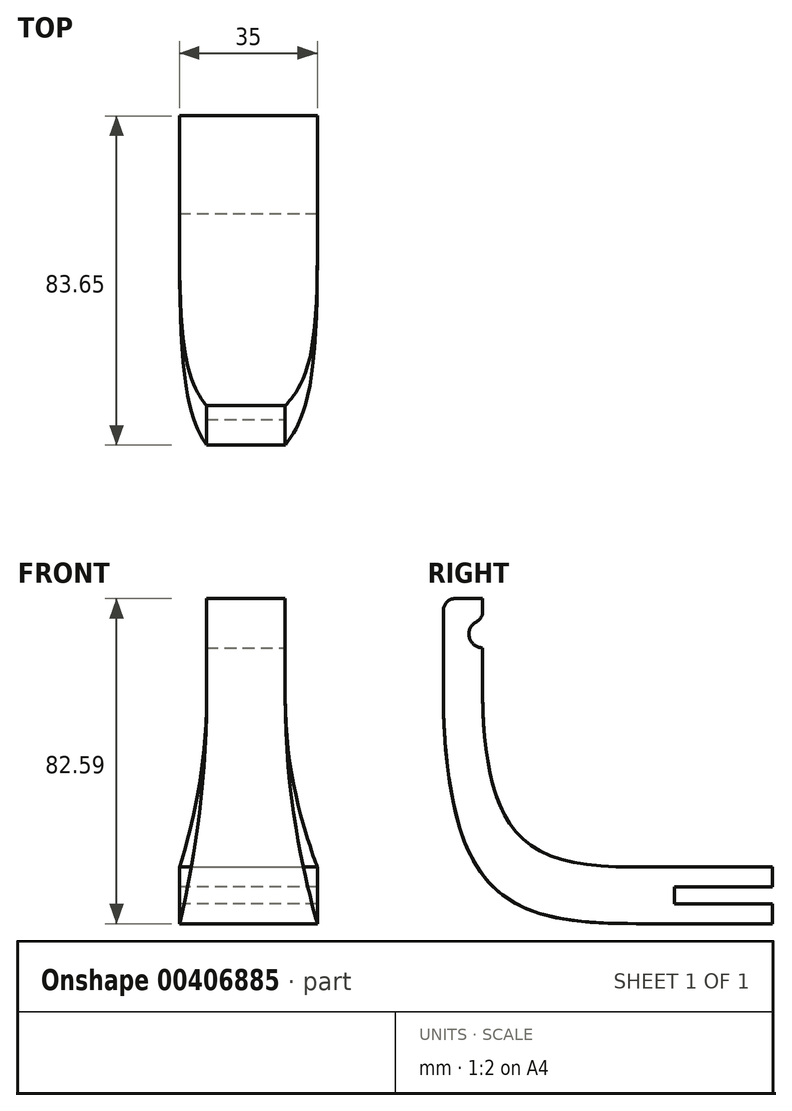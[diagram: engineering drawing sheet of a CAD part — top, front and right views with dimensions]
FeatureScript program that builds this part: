
annotation { "Feature Type Name" : "Feature", "Feature Type Description" : "" }
export const myFeature = defineFeature(function(context is Context, id is Id, definition is map)
    precondition{}
    {
        {
            var Q0;
            Q0=qCreatedBy(makeId("Top.planeOp"),FACE);
            var sketch = newSketch(context, id + "F0", { "sketchPlane" : qUnion([Q0])});
            skLineSegment(sketch, "E0.bottom", {"start": v(-16.82, 18.06) * mm, "end": v(18.18, 18.06) * mm});
            skLineSegment(sketch, "E0.top", {"start": v(-16.82, -13.94) * mm, "end": v(18.18, -13.94) * mm});
            skLineSegment(sketch, "E0.left", {"start": v(-16.82, 18.06) * mm, "end": v(-16.82, -13.94) * mm});
            skLineSegment(sketch, "E0.right", {"start": v(18.18, 18.06) * mm, "end": v(18.18, -13.94) * mm});
            skSolve(sketch);
        }
        {
            var Q0;
            Q0 = qSketchRegion(id + "F0", true);
            extrude(context, id + "F1", {"entities" : qUnion([Q0]), "depth" : 14.4 * mm});
        }
        {
            var Q0;
            Q0=makeQuery(id+"F1.opExtrude","SWEPT_FACE",FACE,{"disambiguationData":[OSD([sQuery(id+"F0.wireOp",EDGE,"E0.bottom")])]});
            var sketch = newSketch(context, id + "F2", { "sketchPlane" : qUnion([Q0])});
            skLineSegment(sketch, "E1.bottom", {"start": v(-18.18, 9.4) * mm, "end": v(16.82, 9.4) * mm});
            skLineSegment(sketch, "E1.top", {"start": v(-18.18, 5) * mm, "end": v(16.82, 5) * mm});
            skLineSegment(sketch, "E1.left", {"start": v(-18.18, 9.4) * mm, "end": v(-18.18, 5) * mm});
            skLineSegment(sketch, "E1.right", {"start": v(16.82, 9.4) * mm, "end": v(16.82, 5) * mm});
            skSolve(sketch);
        }
        {
            var Q0;
            Q0=makeQuery(id+"F2.imprint","IMPRINT",FACE,{"disambiguationData":[TD([[makeQuery(id+"F2.imprint","IMPRINT",EDGE,{"derivedFrom":sQuery(id+"F2.wireOp",EDGE,"E1.bottom")}),-1.0]])]});
            extrude(context, id + "F3", {"entities" : qUnion([Q0]), "operationType" : NewBodyOperationType.REMOVE, "oppositeDirection" : true, "depth" : 25 * mm});
        }
        {
            var Q0;
            Q0=qCreatedBy(makeId("Right.planeOp"),FACE);
            var sketch = newSketch(context, id + "F4", { "sketchPlane" : qUnion([Q0])});
            skLineSegment(sketch, "E2.bottom", {"start": v(-65.6, 82.59) * mm, "end": v(-55.6, 82.59) * mm});
            skLineSegment(sketch, "E2.top", {"start": v(-65.6, 57.59) * mm, "end": v(-55.6, 57.59) * mm});
            skLineSegment(sketch, "E2.left", {"start": v(-65.6, 82.59) * mm, "end": v(-65.6, 57.59) * mm});
            skLineSegment(sketch, "E2.right", {"start": v(-55.6, 82.59) * mm, "end": v(-55.6, 57.59) * mm});
            skSolve(sketch);
        }
        {
            var Q0;
            Q0=makeQuery(id+"F4.imprint","IMPRINT",FACE,{"disambiguationData":[TD([[makeQuery(id+"F4.imprint","IMPRINT",EDGE,{"derivedFrom":sQuery(id+"F4.wireOp",EDGE,"E2.bottom")}),-1.0]])]});
            extrude(context, id + "F5", {"entities" : qUnion([Q0]), "depth" : 10 * mm, "hasSecondDirection" : true, "secondDirectionOppositeDirection" : true, "secondDirectionDepth" : 10 * mm});
        }
        {
            var Q2;
            Q2=makeQuery(id+"F1.opExtrude","SWEPT_FACE",FACE,{"disambiguationData":[OSD([sQuery(id+"F0.wireOp",EDGE,"E0.top")])]});
            var Q3;
            Q3=makeQuery(id+"F5.opExtrude","SWEPT_FACE",FACE,{"disambiguationData":[OSD([sQuery(id+"F4.wireOp",EDGE,"E2.top")])]});
            var Q4;
            Q4=sQuery(id+"F2UIlzxoGKs4pUu_2.wireOp",EDGE,"aDQpYjX3-ybe2-Ym90-JHUU-q4oDbTCzph4g");
            loft(context, id + "F6", {"operationType" : NewBodyOperationType.ADD, "startCondition" : LoftEndDerivativeType.MATCH_CURVATURE, "startMagnitude" : 2.1, "endCondition" : LoftEndDerivativeType.MATCH_TANGENT, "endMagnitude" : 1.8, "sheetProfilesArray" : [{ "sheetProfileEntities" : qUnion([Q2]) }, { "sheetProfileEntities" : qUnion([Q3]) }], "guidesArray" : [{ "guideEntities" : qUnion([Q4]), "guideDerivativeType" : LoftGuideDerivativeType.DEFAULT, "guideDerivativeMagnitude" : 1 }]});
        }
        {
            var Q0;
            Q0=makeQuery(id+"F5.opExtrude","CAP_FACE",FACE,{"disambiguationData":[OSD([sQuery(id+"F4.wireOp",EDGE,"E2.bottom"),sQuery(id+"F4.wireOp",EDGE,"E2.top"),sQuery(id+"F4.wireOp",EDGE,"E2.left"),sQuery(id+"F4.wireOp",EDGE,"E2.right")])],"isStart":false});
            var sketch = newSketch(context, id + "F7", { "sketchPlane" : qUnion([Q0])});
            skCircle(sketch, "E3", {"center": v(-55.6, 73.59) * mm, "radius": 3.5 * mm});
            skSolve(sketch);
        }
        {
            var Q0;
            Q0 = qSketchRegion(id + "F7", true);
            extrude(context, id + "F8", {"entities" : qUnion([Q0]), "operationType" : NewBodyOperationType.REMOVE, "endBound" : BoundingType.UP_TO_NEXT, "oppositeDirection" : true, "depth" : 25 * mm});
        }
        {
            var Q0;
            Q0=makeQuery(id+"F5.opExtrude","SWEPT_EDGE",EDGE,{"disambiguationData":[OSD([sQuery(id+"F4.wireOp",EDGE,"E2.bottom"),sQuery(id+"F4.wireOp",EDGE,"E2.left")])]});
            var Q1;
            Q1=makeQuery(id+"F8.boolean.opBoolean","COPY",EDGE,{"derivedFrom":makeQuery(id+"F8.opExtrude","CAP_EDGE",EDGE,{"disambiguationData":[OSD([sQuery(id+"F7.wireOp",EDGE,"E3")]),topologyDisambiguationEdgeConnected([makeQuery(id+"F5.opExtrude","SWEPT_FACE",FACE,{"disambiguationData":[OSD([sQuery(id+"F4.wireOp",EDGE,"E2.right")])]})]),OD(1.0)],"isStart":false})});
            fillet(context, id + "F9", {"entities" : qUnion([Q0, Q1]), "radius" : 3 * mm, "tangentPropagation" : true, "allowEdgeOverflow" : false});
        }
    });
